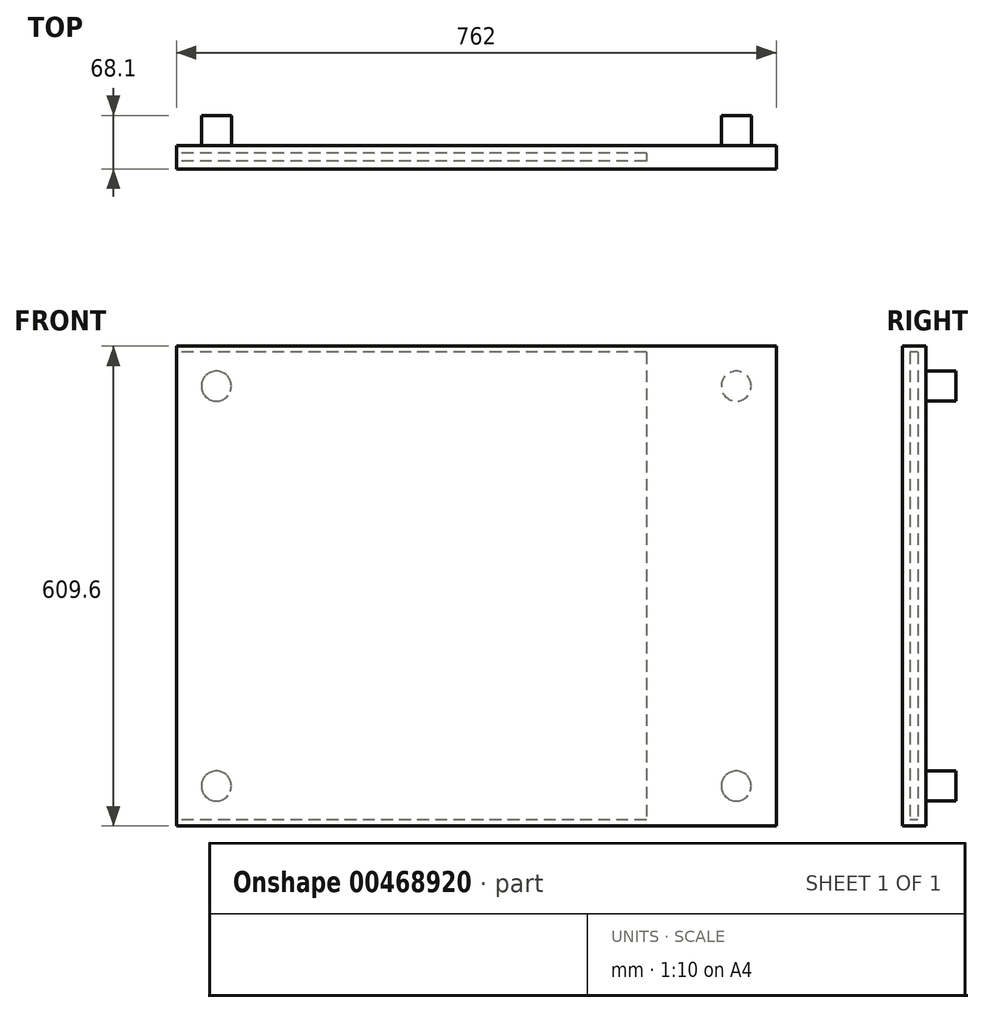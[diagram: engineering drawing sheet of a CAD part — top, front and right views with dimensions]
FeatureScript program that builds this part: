
annotation { "Feature Type Name" : "Feature", "Feature Type Description" : "" }
export const myFeature = defineFeature(function(context is Context, id is Id, definition is map)
    precondition{}
    {
        {
            var Q0;
            Q0=qCreatedBy(makeId("Front.planeOp"),FACE);
            var sketch = newSketch(context, id + "F0", { "sketchPlane" : qUnion([Q0])});
            skLineSegment(sketch, "E0.bottom", {"start": v(381, -304.8) * mm, "end": v(-381, -304.8) * mm});
            skLineSegment(sketch, "E0.top", {"start": v(381, 304.8) * mm, "end": v(-381, 304.8) * mm});
            skLineSegment(sketch, "E0.left", {"start": v(381, -304.8) * mm, "end": v(381, 304.8) * mm});
            skLineSegment(sketch, "E0.right", {"start": v(-381, -304.8) * mm, "end": v(-381, 304.8) * mm});
            skPoint(sketch, "E0.middle", {"position": v(0, 0) * mm});
            skSolve(sketch);
        }
        {
            var Q0;
            Q0=makeQuery(id+"F0.imprint","IMPRINT",FACE,{"disambiguationData":[TD([[makeQuery(id+"F0.imprint","IMPRINT",EDGE,{"derivedFrom":sQuery(id+"F0.wireOp",EDGE,"E0.bottom")}),-1.0]])]});
            extrude(context, id + "F1", {"entities" : qUnion([Q0]), "depth" : 30 * mm});
        }
        {
            var Q0;
            Q0=makeQuery(id+"F1.opExtrude","SWEPT_FACE",FACE,{"disambiguationData":[OSD([sQuery(id+"F0.wireOp",EDGE,"E0.right")])]});
            var sketch = newSketch(context, id + "F2", { "sketchPlane" : qUnion([Q0])});
            skLineSegment(sketch, "E1.bottom", {"start": v(10, 297.18) * mm, "end": v(20, 297.18) * mm});
            skLineSegment(sketch, "E1.top", {"start": v(10, -297.18) * mm, "end": v(20, -297.18) * mm});
            skLineSegment(sketch, "E1.left", {"start": v(10, 297.18) * mm, "end": v(10, -297.18) * mm});
            skLineSegment(sketch, "E1.right", {"start": v(20, 297.18) * mm, "end": v(20, -297.18) * mm});
            skSolve(sketch);
        }
        {
            var Q0;
            Q0=makeQuery(id+"F2.imprint","IMPRINT",FACE,{"disambiguationData":[TD([[makeQuery(id+"F2.imprint","IMPRINT",EDGE,{"derivedFrom":sQuery(id+"F2.wireOp",EDGE,"E1.bottom")}),-1.0]])]});
            extrude(context, id + "F3", {"entities" : qUnion([Q0]), "operationType" : NewBodyOperationType.REMOVE, "oppositeDirection" : true, "depth" : 596.9 * mm});
        }
        {
            var Q0;
            Q0=makeQuery(id+"F1.opExtrude","CAP_FACE",FACE,{"disambiguationData":[OSD([sQuery(id+"F0.wireOp",EDGE,"E0.bottom"),sQuery(id+"F0.wireOp",EDGE,"E0.top"),sQuery(id+"F0.wireOp",EDGE,"E0.left"),sQuery(id+"F0.wireOp",EDGE,"E0.right")])],"isStart":true});
            var sketch = newSketch(context, id + "F4", { "sketchPlane" : qUnion([Q0])});
            skCircle(sketch, "E2", {"center": v(-330.2, 254) * mm, "radius": 19.05 * mm});
            skCircle(sketch, "E3", {"center": v(330.2, 254) * mm, "radius": 19.05 * mm});
            skCircle(sketch, "E4", {"center": v(330.2, -254) * mm, "radius": 19.05 * mm});
            skCircle(sketch, "E5", {"center": v(-330.2, -254) * mm, "radius": 19.05 * mm});
            skSolve(sketch);
        }
        {
            var Q0;
            Q0 = qSketchRegion(id + "F4", true);
            extrude(context, id + "F5", {"entities" : qUnion([Q0]), "operationType" : NewBodyOperationType.ADD, "depth" : 38.1 * mm});
        }
    });
